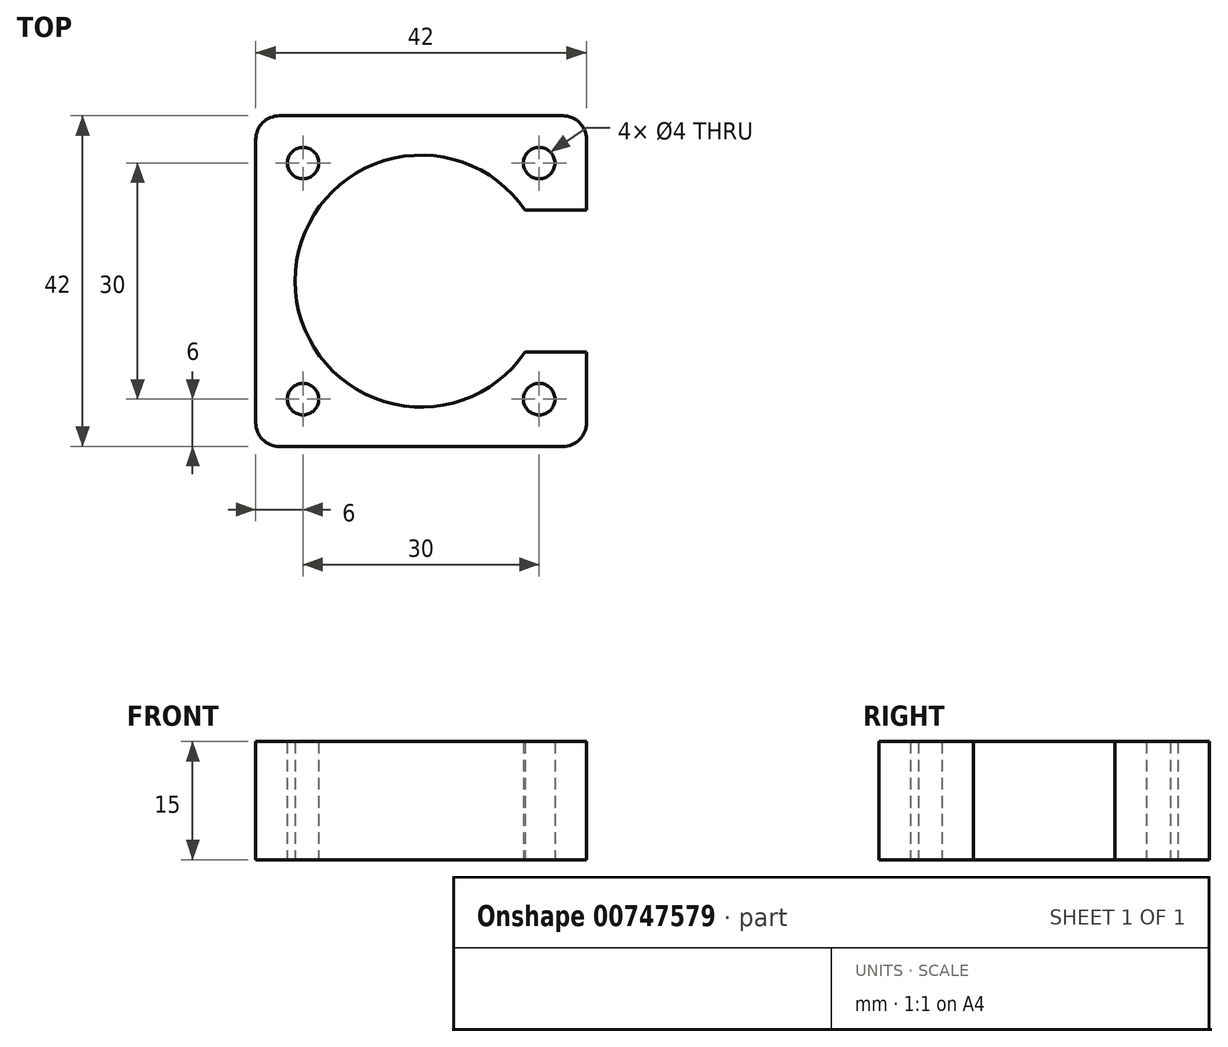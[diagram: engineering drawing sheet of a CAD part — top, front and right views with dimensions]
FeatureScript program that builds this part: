
annotation { "Feature Type Name" : "Feature", "Feature Type Description" : "" }
export const myFeature = defineFeature(function(context is Context, id is Id, definition is map)
    precondition{}
    {
        {
            var Q0;
            Q0=qCreatedBy(makeId("Top.planeOp"),FACE);
            var sketch = newSketch(context, id + "F0", { "sketchPlane" : qUnion([Q0])});
            skLineSegment(sketch, "E0.bottom", {"start": v(18, -21) * mm, "end": v(-18, -21) * mm});
            skLineSegment(sketch, "E0.top", {"start": v(18, 21) * mm, "end": v(-18, 21) * mm});
            skLineSegment(sketch, "E0.left", {"start": v(21, -18) * mm, "end": v(21, 18) * mm});
            skLineSegment(sketch, "E0.right", {"start": v(-21, -18) * mm, "end": v(-21, 18) * mm});
            skPoint(sketch, "E0.middle", {"position": v(0, 0) * mm});
            skCircle(sketch, "E1", {"center": v(0, 0) * mm, "radius": 16 * mm});
            skCircle(sketch, "E2", {"center": v(-15, 15) * mm, "radius": 2 * mm});
            skCircle(sketch, "E3", {"center": v(-15, -15) * mm, "radius": 2 * mm});
            skCircle(sketch, "E4", {"center": v(15, 15) * mm, "radius": 2 * mm});
            skCircle(sketch, "E5", {"center": v(15, -15) * mm, "radius": 2 * mm});
            skLineSegment(sketch, "E6", {"start": v(-21, -15) * mm, "end": v(21, -15) * mm, "construction": true});
            skLineSegment(sketch, "E7", {"start": v(-21, 15) * mm, "end": v(21, 15) * mm, "construction": true});
            skPoint(sketch, "E8.visualSharp", {"position": v(-21, 21) * mm});
            skArc(sketch, "E8.filletArc", {"start": v(-18, 21) * mm, "mid": v(-20.12, 20.12) * mm, "end": v(-21, 18) * mm});
            skPoint(sketch, "E9.visualSharp", {"position": v(-21, -21) * mm});
            skArc(sketch, "E9.filletArc", {"start": v(-21, -18) * mm, "mid": v(-20.12, -20.12) * mm, "end": v(-18, -21) * mm});
            skPoint(sketch, "E10.visualSharp", {"position": v(21, -21) * mm});
            skArc(sketch, "E10.filletArc", {"start": v(18, -21) * mm, "mid": v(20.12, -20.12) * mm, "end": v(21, -18) * mm});
            skPoint(sketch, "E11.visualSharp", {"position": v(21, 21) * mm});
            skArc(sketch, "E11.filletArc", {"start": v(21, 18) * mm, "mid": v(20.12, 20.12) * mm, "end": v(18, 21) * mm});
            skSolve(sketch);
        }
        {
            var Q0;
            Q0=makeQuery(id+"F0.imprint","IMPRINT",FACE,{"disambiguationData":[TD([[makeQuery(id+"F0.imprint","IMPRINT",EDGE,{"derivedFrom":sQuery(id+"F0.wireOp",EDGE,"E0.bottom")}),-1.0]])]});
            extrude(context, id + "F1", {"entities" : qUnion([Q0]), "depth" : 15 * mm, "offsetDistance" : 25 * mm});
        }
        {
            var Q0;
            Q0=qCreatedBy(makeId("Top.planeOp"),FACE);
            var sketch = newSketch(context, id + "F2", { "sketchPlane" : qUnion([Q0])});
            skLineSegment(sketch, "E12.bottom", {"start": v(0, 9) * mm, "end": v(31.5, 9) * mm});
            skLineSegment(sketch, "E12.top", {"start": v(0, -9) * mm, "end": v(31.5, -9) * mm});
            skLineSegment(sketch, "E12.left", {"start": v(0, 9) * mm, "end": v(0, -9) * mm});
            skLineSegment(sketch, "E12.right", {"start": v(31.5, 9) * mm, "end": v(31.5, -9) * mm});
            skSolve(sketch);
        }
        {
            var Q0;
            Q0 = qSketchRegion(id + "F2", true);
            extrude(context, id + "F3", {"entities" : qUnion([Q0]), "operationType" : NewBodyOperationType.REMOVE, "endBound" : BoundingType.THROUGH_ALL, "depth" : 25 * mm, "offsetDistance" : 25 * mm});
        }
    });
